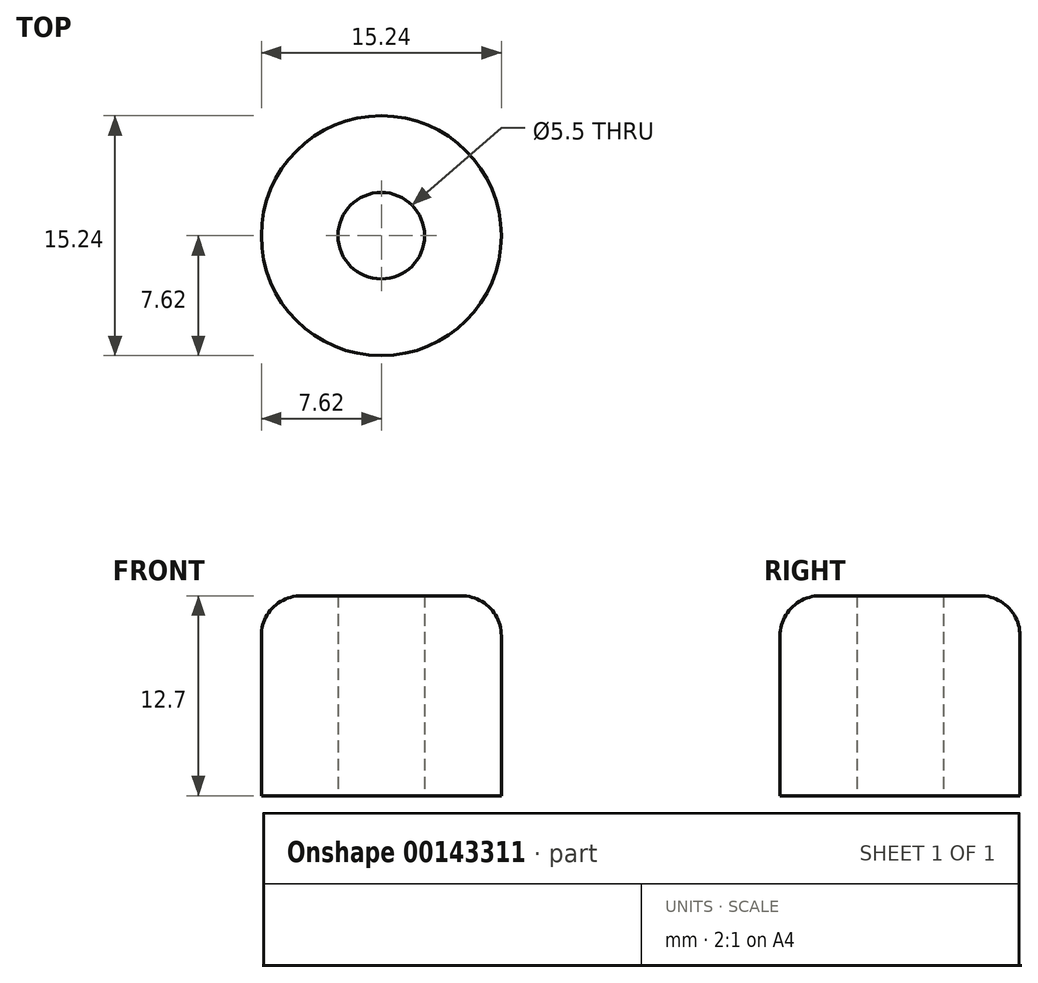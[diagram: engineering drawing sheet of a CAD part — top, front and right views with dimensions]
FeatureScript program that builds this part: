
annotation { "Feature Type Name" : "Feature", "Feature Type Description" : "" }
export const myFeature = defineFeature(function(context is Context, id is Id, definition is map)
    precondition{}
    {
        {
            var Q0;
            Q0=qCreatedBy(makeId("Front.planeOp"),FACE);
            var sketch = newSketch(context, id + "F0", { "sketchPlane" : qUnion([Q0])});
            skLineSegment(sketch, "E0", {"start": v(0, 0) * mm, "end": v(0, 12.8) * mm, "construction": true});
            skLineSegment(sketch, "E1", {"start": v(2.75, 12.7) * mm, "end": v(5.08, 12.7) * mm});
            skLineSegment(sketch, "E2", {"start": v(7.62, 10.16) * mm, "end": v(7.62, 0) * mm});
            skLineSegment(sketch, "E3", {"start": v(7.62, 0) * mm, "end": v(2.75, 0) * mm});
            skLineSegment(sketch, "E4", {"start": v(2.75, 0) * mm, "end": v(2.75, 12.7) * mm});
            skPoint(sketch, "E5.visualSharp", {"position": v(7.62, 12.7) * mm});
            skArc(sketch, "E5.filletArc", {"start": v(7.62, 10.16) * mm, "mid": v(6.88, 11.96) * mm, "end": v(5.08, 12.7) * mm});
            skSolve(sketch);
        }
        {
            var Q0;
            Q0 = qSketchRegion(id + "F0", true);
            var Q1;
            Q1=sQuery(id+"F0.wireOp",EDGE,"E0");
            revolve(context, id + "F1", {"surfaceOperationType" : NewSurfaceOperationType.NEW, "entities" : qUnion([Q0]), "axis" : qUnion([Q1]), "revolveType" : RevolveType.FULL});
        }
    });
